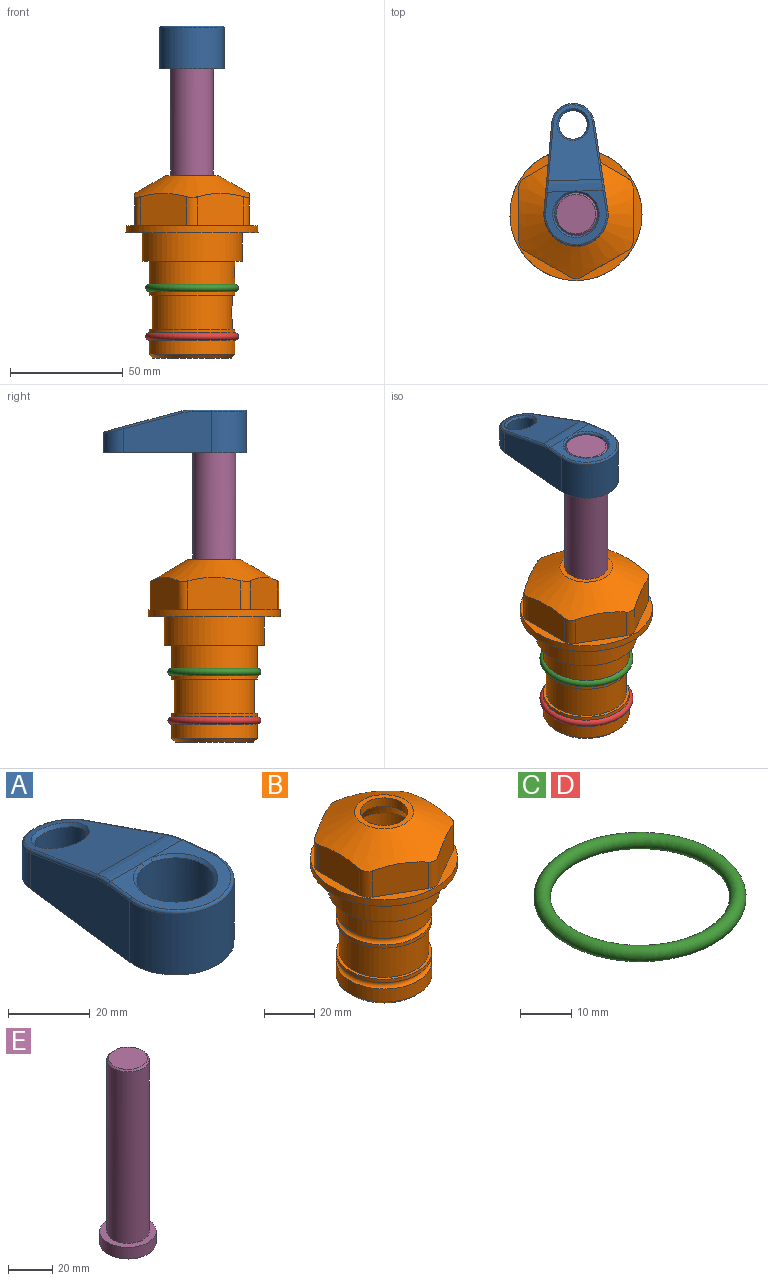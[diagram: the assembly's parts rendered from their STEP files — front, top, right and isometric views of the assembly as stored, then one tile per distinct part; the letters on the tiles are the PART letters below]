
ASSEMBLY  parts=5 mates=4
PART A: 31 faces, bbox 31.7x65.5x19.8 mm
  f0: plane 39.12x18.26mm, normal (0.99,0.12,0), area 612.2mm2, adj f1,f4,f7,f11,f13,f15
  f1: cylinder r=9.53mm len=18.91mm, axis (0,0,-1), area 296.1mm2, adj f0,f2,f7,f17
  f2: plane 39.12x18.26mm, normal (-0.99,0.12,0), area 612.2mm2, adj f1,f4,f7,f12,f14,f16
  f3: cylinder r=6.35mm len=12.7mm, axis (0,0,-1), area 362.4mm2, adj f7,f18
  f4: cylinder r=14.29mm len=28.58mm, axis (0,0,-1), area 882.2mm2, adj f0,f2,f7,f10
  f5: cylinder r=9.53mm len=19.05mm, axis (0,0,-1), area 1092.6mm2, adj f7,f19,f20
  f6: plane 26.99x23.69mm, normal (0,0,1), area 216.2mm2, adj f9,f10,f11,f12,f19
  f7: plane 63.5x28.58mm, normal (0,0,-1), area 661.8mm2, adj f0,f1,f2,f3,f4,f5,f22,f23
  f8: plane 33.52x23.6mm, normal (0,0.26,0.97), area 486mm2, adj f9,f15,f16,f17,f18
  f9: cylinder r=19.05mm len=24.72mm, axis (1,0,0), area 120.4mm2, adj f6,f8,f13,f14,f20
  f10: torus R=13.49mm, axis (0,0,1), area 59mm2, adj f4,f6,f11,f12
  f11: cylinder r=0.79mm len=8.67mm, axis (0.12,-0.99,0), area 10.8mm2, adj f0,f6,f10,f13
  f12: cylinder r=0.79mm len=8.67mm, axis (0.12,0.99,0), area 10.8mm2, adj f2,f6,f10,f14
  f13: bspline ~4.95x1.42mm, area 6.1mm2, adj f0,f9,f11,f15
  f14: bspline ~4.95x1.42mm, area 6.1mm2, adj f2,f9,f12,f16
  f15: cylinder r=0.79mm len=25.95mm, axis (0.12,-0.96,0.26), area 32.9mm2, adj f0,f8,f13,f17
  f16: cylinder r=0.79mm len=25.95mm, axis (0.12,0.96,-0.26), area 32.9mm2, adj f2,f8,f14,f17
  f17: bspline ~18.91x8.38mm, area 30mm2, adj f1,f8,f15,f16
  f18: bspline ~14.29x14.29mm, area 48.3mm2, adj f3,f8
  f19: cone r=9.53mm half-angle=45deg, axis (0,0,1), area 66.5mm2, adj f5,f6,f20
  f20: bspline ~3.22x0.96mm, area 3.5mm2, adj f5,f9,f19
  f21: plane 2.75x2.72mm, normal (0,0,-1), area 2.9mm2, adj f23,f25,f28
  f22: plane 23.05x15.88mm, normal (-0.99,-0.12,0), area 323.6mm2, adj f7,f25,f26,f27,f28,f29
  f23: plane 23.05x15.88mm, normal (0.99,-0.12,0), area 323.6mm2, adj f7,f21,f25,f27,f28,f30
  f24: cylinder r=9.53mm len=10.69mm, axis (0,0,-1), area 114.7mm2, adj f7,f27,f29,f30
  f25: cylinder r=12.7mm len=20.59mm, axis (0,0,-1), area 381.1mm2, adj f7,f21,f22,f23,f26,f28
  f26: plane 2.75x2.72mm, normal (0,0,-1), area 2.9mm2, adj f22,f25,f28
  f27: plane 19.72x18.37mm, normal (0,-0.26,-0.97), area 291.8mm2, adj f22,f23,f24,f28,f29,f30
  f28: cylinder r=15.88mm len=19.92mm, axis (1,0,0), area 54.8mm2, adj f21,f22,f23,f25,f26,f27
  f29: cylinder r=1.59mm len=11mm, axis (0,0,-1), area 34.7mm2, adj f7,f22,f24,f27
  f30: cylinder r=1.59mm len=11mm, axis (0,0,-1), area 34.7mm2, adj f7,f23,f24,f27
PART B: 36 faces, bbox 58.7x58.7x81 mm
  f0: cylinder r=17.78mm len=35.56mm, axis (0,0,1), area 1670.8mm2, adj f23,f24,f31
  f1: cylinder r=19.05mm len=38.1mm, axis (0,0,1), area 1191.9mm2, adj f26,f27,f30
  f2: plane 58.66x58.66mm, normal (0,0,-1), area 1150.6mm2, adj f3,f28
  f3: cylinder r=29.33mm len=58.66mm, axis (0,0,-1), area 585.1mm2, adj f2,f4
  f4: plane 58.66x58.66mm, normal (0,0,1), area 475.9mm2, adj f3,f5,f6,f7,f8,f9,f10,f11
  f5: plane 20.32x14.34mm, normal (-0.5,0.87,0), area 324.4mm2, adj f4,f15,f16,f17
  f6: plane 20.32x14.34mm, normal (0.5,0.87,0), area 324.4mm2, adj f4,f14,f15,f17
  f7: plane 23.48x14.34mm, normal (1,0,0), area 324.4mm2, adj f4,f13,f14,f17
  f8: plane 20.32x14.34mm, normal (0.5,-0.87,0), area 324.4mm2, adj f4,f12,f13,f17
  f9: plane 20.32x14.34mm, normal (-0.5,-0.87,0), area 324.4mm2, adj f4,f11,f12,f17
  f10: plane 23.48x14.34mm, normal (-1,0,0), area 324.4mm2, adj f4,f11,f16,f17
  f11: cylinder r=5.08mm len=12.85mm, axis (0,0,-1), area 67.2mm2, adj f4,f9,f10,f17
  f12: cylinder r=5.08mm len=12.85mm, axis (0,0,-1), area 67.2mm2, adj f4,f8,f9,f17
  f13: cylinder r=5.08mm len=12.85mm, axis (0,0,-1), area 67.2mm2, adj f4,f7,f8,f17
  f14: cylinder r=5.08mm len=12.85mm, axis (0,0,-1), area 67.2mm2, adj f4,f6,f7,f17
  f15: cylinder r=5.08mm len=12.85mm, axis (0,0,-1), area 67.2mm2, adj f4,f5,f6,f17
  f16: cylinder r=5.08mm len=12.85mm, axis (0,0,-1), area 67.2mm2, adj f4,f5,f10,f17
  f17: cone r=11.73mm half-angle=60deg, axis (0,0,-1), area 2071.8mm2, adj f5,f6,f7,f8,f9,f10,f11,f12
  f18: plane 23.46x23.46mm, normal (0,0,1), area 147.4mm2, adj f17,f35
  f19: plane 34.93x34.93mm, normal (0,0,-1), area 958mm2, adj f29
  f20: cylinder r=19.05mm len=38.1mm, axis (0,0,1), area 760.1mm2, adj f21,f29
  f21: torus R=19.05mm, axis (0,0,1), area 565.3mm2, adj f20,f22
  f22: cylinder r=19.05mm len=38.1mm, axis (0,0,1), area 190mm2, adj f21,f23
  f23: plane 38.1x38.1mm, normal (0,0,1), area 146.9mm2, adj f0,f22
  f24: plane 38.1x38.1mm, normal (0,0,-1), area 146.9mm2, adj f0,f25
  f25: cylinder r=19.05mm len=38.1mm, axis (0,0,1), area 190mm2, adj f24,f26
  f26: torus R=19.05mm, axis (0,0,1), area 565.3mm2, adj f1,f25
  f27: plane 44.45x44.45mm, normal (0,0,-1), area 411.7mm2, adj f1,f28
  f28: cylinder r=22.23mm len=44.45mm, axis (0,0,1), area 1773.5mm2, adj f2,f27
  f29: cone r=19.05mm half-angle=45deg, axis (0,0,1), area 257.5mm2, adj f19,f20
  f30: cylinder r=3.17mm len=6.75mm, axis (-1,0,0), area 128mm2, adj f1,f33
  f31: cylinder r=3.17mm len=6.35mm, axis (-1,0,0), area 102.5mm2, adj f0,f33
  f32: plane 25.4x25.4mm, normal (0,0,1), area 506.7mm2, adj f33
  f33: cylinder r=12.7mm len=66.42mm, axis (0,0,-1), area 5236.2mm2, adj f30,f31,f32,f34
  f34: cone r=9.53mm half-angle=30deg, axis (0,0,-1), area 443.4mm2, adj f33,f35
  f35: cylinder r=9.53mm len=19.05mm, axis (0,0,-1), area 240.9mm2, adj f18,f34
PART C: 1 faces, bbox 44.7x44.7x3.2 mm
  f0: torus R=19.05mm, axis (0,0,1), area 1193.9mm2
PART D: same geometry as C
PART E: 6 faces, bbox 25.4x25.4x101.6 mm
  f0: plane 17.46x17.46mm, normal (0,0,1), area 239.5mm2, adj f5
  f1: plane 25.4x25.4mm, normal (0,0,-1), area 506.7mm2, adj f2
  f2: cylinder r=12.7mm len=25.4mm, axis (0,0,1), area 506.7mm2, adj f1,f3
  f3: plane 25.4x25.4mm, normal (0,0,1), area 221.7mm2, adj f2,f4
  f4: cylinder r=9.53mm len=94.46mm, axis (0,0,1), area 5653mm2, adj f3,f5
  f5: cone r=8.73mm half-angle=45deg, axis (0,0,-1), area 64.4mm2, adj f0,f4
PLACE A rot(axis=(0,0,1),1.9deg) t=(0,0,28.35)mm
PLACE B at identity fixed
PLACE C at identity
PLACE D t=(0,0,-21.59)mm
PLACE E rot(axis=(0,0,1),1.9deg) t=(0,0,27.55)mm
MATE fastened B.f0 <-> C.f0  axis (0,0,1) through (0,0,-24.51)mm
MATE cylindrical B.f0 <-> E.f2  axis (0,0,1) through (0,0,-50.55)mm
MATE fastened B.f0 <-> D.f0  axis (0,0,1) through (0,0,-46.1)mm
MATE fastened A.f4 <-> E.f2  axis (0,0,-1) through (0,0,91.05)mm
